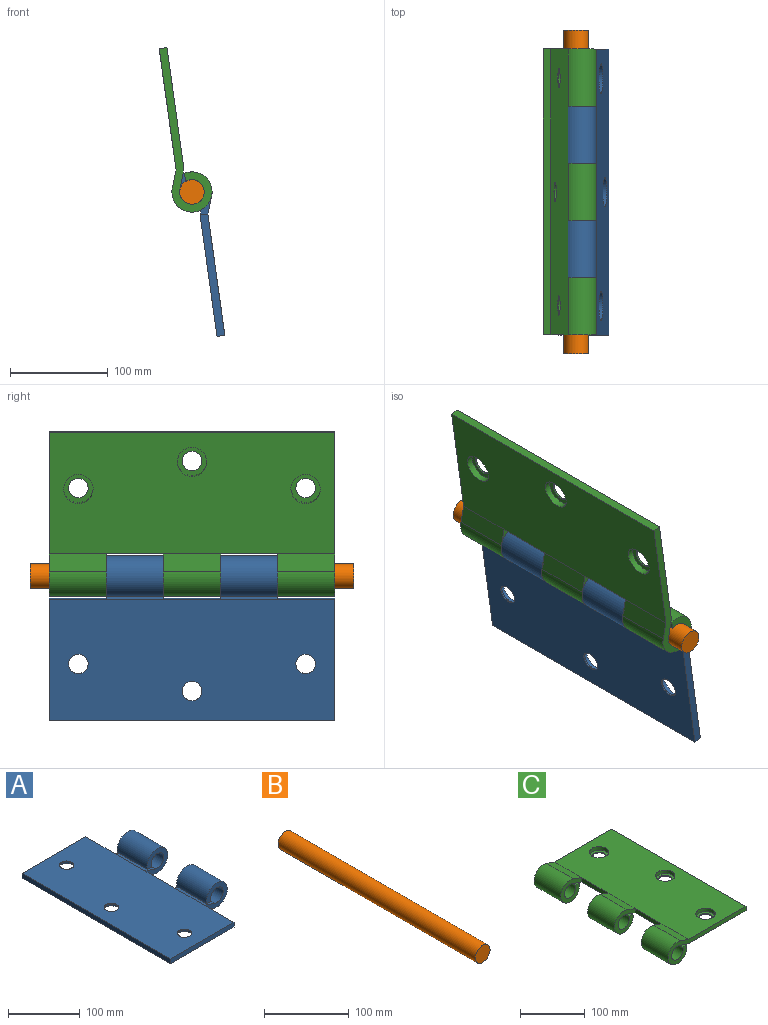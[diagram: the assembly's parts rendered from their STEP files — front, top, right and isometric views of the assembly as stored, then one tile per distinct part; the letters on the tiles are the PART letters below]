
ASSEMBLY  parts=3 mates=2
PART A: 31 faces, bbox 170x292x41 mm
  f0: plane 58.4x8.42mm, normal (0,0,-1), area 492mm2, adj f2,f8,f28,f30
  f1: plane 58.4x8.42mm, normal (0,0,-1), area 492mm2, adj f3,f9,f25,f27
  f2: cylinder r=12.5mm len=58.4mm, axis (0,1,0), area 3975.6mm2, adj f0,f4,f28,f30
  f3: cylinder r=12.5mm len=58.4mm, axis (0,1,0), area 3975.6mm2, adj f1,f5,f25,f27
  f4: plane 58.4x20.54mm, normal (0.32,0,0.95), area 1264.7mm2, adj f2,f10,f28,f30
  f5: plane 58.4x20.54mm, normal (0.32,0,0.95), area 1264.7mm2, adj f3,f10,f25,f27
  f6: plane 58.4x17.59mm, normal (-0.34,0,-0.94), area 1091mm2, adj f8,f12,f28,f30
  f7: plane 58.4x17.59mm, normal (-0.34,0,-0.94), area 1091mm2, adj f9,f12,f25,f27
  f8: cylinder r=20.5mm len=58.4mm, axis (0,1,0), area 6348.4mm2, adj f0,f6,f28,f30
  f9: cylinder r=20.5mm len=58.4mm, axis (0,1,0), area 6348.4mm2, adj f1,f7,f25,f27
  f10: plane 292x125mm, normal (0,0,1), area 35557.5mm2, adj f4,f5,f11,f13,f14,f15,f18,f21
  f11: plane 292x8mm, normal (-1,0,0), area 2336mm2, adj f10,f12,f13,f14
  f12: plane 292x125mm, normal (0,0,-1), area 34379.4mm2, adj f6,f7,f11,f13,f14,f17,f20,f23
  f13: plane 125x8mm, normal (0,-1,0), area 1000mm2, adj f10,f11,f12,f29
  f14: plane 125x8mm, normal (0,1,0), area 1000mm2, adj f10,f11,f12,f24
  f15: cylinder r=10mm len=20mm, axis (0,0,-1), area 94.2mm2, adj f10,f16
  f16: plane 30x30mm, normal (0,0,-1), area 392.7mm2, adj f15,f17
  f17: cylinder r=15mm len=30mm, axis (0,0,-1), area 612.6mm2, adj f12,f16
  f18: cylinder r=10mm len=20mm, axis (0,0,-1), area 94.2mm2, adj f10,f19
  f19: plane 30x30mm, normal (0,0,-1), area 392.7mm2, adj f18,f20
  f20: cylinder r=15mm len=30mm, axis (0,0,-1), area 612.6mm2, adj f12,f19
  f21: cylinder r=10mm len=20mm, axis (0,0,-1), area 94.2mm2, adj f10,f22
  f22: plane 30x30mm, normal (0,0,-1), area 392.7mm2, adj f21,f23
  f23: cylinder r=15mm len=30mm, axis (0,0,-1), area 612.6mm2, adj f12,f22
  f24: plane 58.4x8mm, normal (1,0,0), area 467.2mm2, adj f10,f12,f14,f25
  f25: plane 45x41mm, normal (0,1,0), area 864mm2, adj f1,f3,f5,f7,f9,f24
  f26: plane 58.4x8mm, normal (1,0,0), area 467.2mm2, adj f10,f12,f27,f28
  f27: plane 45x41mm, normal (0,-1,0), area 864mm2, adj f1,f3,f5,f7,f9,f26
  f28: plane 45x41mm, normal (0,1,0), area 864mm2, adj f0,f2,f4,f6,f8,f26
  f29: plane 58.4x8mm, normal (1,0,0), area 467.2mm2, adj f10,f12,f13,f30
  f30: plane 45x41mm, normal (0,-1,0), area 864mm2, adj f0,f2,f4,f6,f8,f29
PART B: 3 faces, bbox 24.8x330x24.8 mm
  f0: cylinder r=12.39mm len=330mm, axis (0,1,0), area 25685.8mm2, adj f1,f2
  f1: plane 24.78x24.78mm, normal (0,-1,0), area 482.1mm2, adj f0
  f2: plane 24.78x24.78mm, normal (0,1,0), area 482.1mm2, adj f0
PART C: 35 faces, bbox 170x292x41 mm
  f0: plane 58.4x8.42mm, normal (0,0,1), area 492mm2, adj f2,f8,f30,f34
  f1: plane 58.4x8.42mm, normal (0,0,1), area 492mm2, adj f3,f9,f18,f31
  f2: cylinder r=12.5mm len=58.4mm, axis (0,-1,0), area 3975.6mm2, adj f0,f4,f30,f34
  f3: cylinder r=12.5mm len=58.4mm, axis (0,-1,0), area 3975.6mm2, adj f1,f5,f18,f31
  f4: plane 58.4x20.54mm, normal (-0.32,0,-0.95), area 1264.7mm2, adj f2,f13,f30,f34
  f5: plane 58.4x20.54mm, normal (-0.32,0,-0.95), area 1264.7mm2, adj f3,f13,f18,f31
  f6: plane 58.4x17.59mm, normal (0.34,0,0.94), area 1091mm2, adj f8,f15,f30,f34
  f7: plane 58.4x17.59mm, normal (0.34,0,0.94), area 1091mm2, adj f9,f15,f18,f31
  f8: cylinder r=20.5mm len=58.4mm, axis (0,-1,0), area 6348.4mm2, adj f0,f6,f30,f34
  f9: cylinder r=20.5mm len=58.4mm, axis (0,-1,0), area 6348.4mm2, adj f1,f7,f18,f31
  f10: plane 58.4x8.42mm, normal (0,0,1), area 492mm2, adj f11,f17,f19,f33
  f11: cylinder r=12.5mm len=58.4mm, axis (0,-1,0), area 3975.6mm2, adj f10,f12,f19,f33
  f12: plane 58.4x20.54mm, normal (-0.32,0,-0.95), area 1264.7mm2, adj f11,f13,f19,f33
  f13: plane 292x125mm, normal (0,0,-1), area 35557.5mm2, adj f4,f5,f12,f14,f18,f19,f20,f23
  f14: plane 292x8mm, normal (1,0,0), area 2336mm2, adj f13,f15,f18,f19
  f15: plane 292x125mm, normal (0,0,1), area 34379.4mm2, adj f6,f7,f14,f16,f18,f19,f22,f25
  f16: plane 58.4x17.59mm, normal (0.34,0,0.94), area 1091mm2, adj f15,f17,f19,f33
  f17: cylinder r=20.5mm len=58.4mm, axis (0,-1,0), area 6348.4mm2, adj f10,f16,f19,f33
  f18: plane 170x41mm, normal (0,1,0), area 1864mm2, adj f1,f3,f5,f7,f9,f13,f14,f15
  f19: plane 170x41mm, normal (0,-1,0), area 1864mm2, adj f10,f11,f12,f13,f14,f15,f16,f17
  f20: cylinder r=10mm len=20mm, axis (0,0,1), area 94.2mm2, adj f13,f21
  f21: plane 30x30mm, normal (0,0,1), area 392.7mm2, adj f20,f22
  f22: cylinder r=15mm len=30mm, axis (0,0,1), area 612.6mm2, adj f15,f21
  f23: cylinder r=10mm len=20mm, axis (0,0,1), area 94.2mm2, adj f13,f24
  f24: plane 30x30mm, normal (0,0,1), area 392.7mm2, adj f23,f25
  f25: cylinder r=15mm len=30mm, axis (0,0,1), area 612.6mm2, adj f15,f24
  f26: cylinder r=10mm len=20mm, axis (0,0,1), area 94.2mm2, adj f13,f27
  f27: plane 30x30mm, normal (0,0,1), area 392.7mm2, adj f26,f28
  f28: cylinder r=15mm len=30mm, axis (0,0,1), area 612.6mm2, adj f15,f27
  f29: plane 58.4x8mm, normal (-1,0,0), area 467.2mm2, adj f13,f15,f30,f31
  f30: plane 45x41mm, normal (0,1,0), area 864mm2, adj f0,f2,f4,f6,f8,f29
  f31: plane 45x41mm, normal (0,-1,0), area 864mm2, adj f1,f3,f5,f7,f9,f29
  f32: plane 58.4x8mm, normal (-1,0,0), area 467.2mm2, adj f13,f15,f33,f34
  f33: plane 45x41mm, normal (0,1,0), area 864mm2, adj f10,f11,f12,f16,f17,f32
  f34: plane 45x41mm, normal (0,-1,0), area 864mm2, adj f0,f2,f4,f6,f8,f32
PLACE A rot(axis=(0,-1,0),97.9deg) t=(-707.11,395.3,-280.12)mm
PLACE B rot(axis=(0,-1,0),7.9deg) t=(-737.04,384.3,-264.6)mm fixed
PLACE C rot(axis=(0,-1,0),97.9deg) t=(-679.38,394.3,-276.26)mm
MATE revolute C.f2 <-> B.f0  axis (0,-1,0) through (-715.44,249.3,-256.55)mm
MATE revolute A.f2 <-> C.f2  axis (0,1,0) through (-715.44,336.9,-256.55)mm
